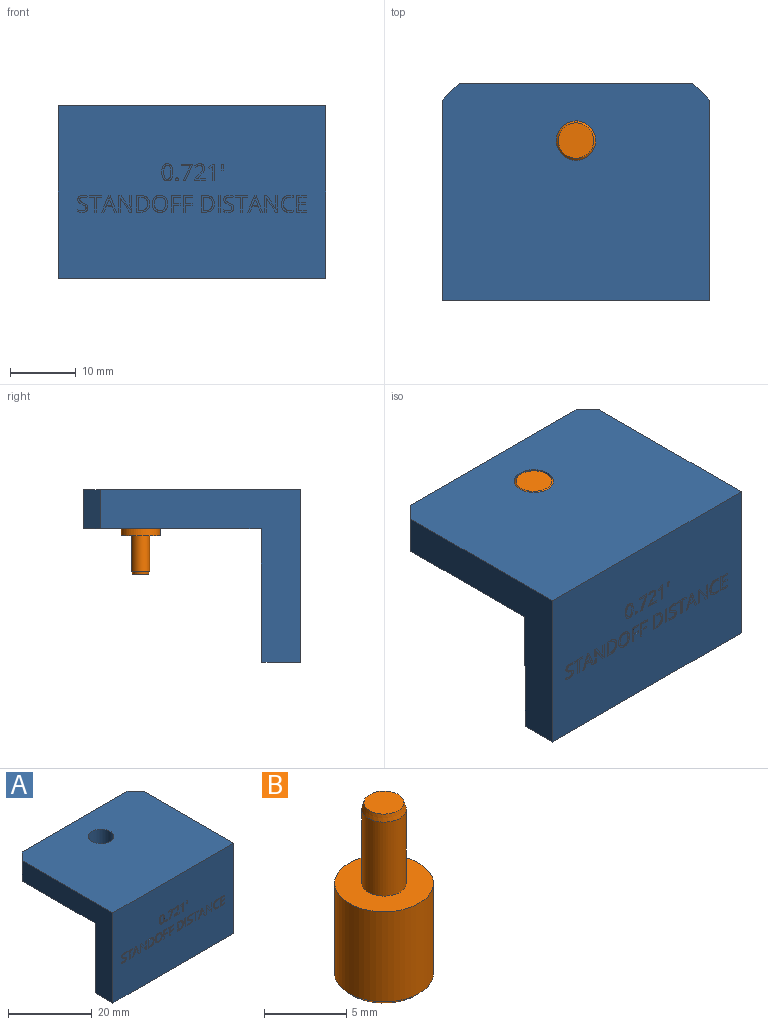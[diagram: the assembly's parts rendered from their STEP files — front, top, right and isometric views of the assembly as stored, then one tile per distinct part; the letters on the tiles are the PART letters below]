
ASSEMBLY  parts=2 mates=1
PART A: 322 faces, bbox 40.6x33x26.3 mm
  f0: plane 40.64x5.87mm, normal (0,0,-1), area 238.5mm2, adj f2,f3,f5,f320
  f1: plane 40.64x9.14mm, normal (0,1,0), area 371.6mm2, adj f2,f4,f5,f321
  f2: plane 30.48x26.32mm, normal (-1,0,0), area 303.3mm2, adj f0,f1,f3,f4,f7,f318,f320,f321
  f3: plane 40.64x26.32mm, normal (0,-1,0), area 1028.5mm2, adj f0,f2,f5,f7,f9,f10,f11,f12
  f4: plane 40.64x27.02mm, normal (0,0,-1), area 1063.4mm2, adj f1,f2,f5,f6,f8,f318,f319
  f5: plane 30.48x26.32mm, normal (1,0,0), area 303.3mm2, adj f0,f1,f3,f4,f7,f319,f320,f321
  f6: plane 35.56x6mm, normal (0,1,0), area 213.4mm2, adj f4,f7,f318,f319
  f7: plane 40.64x33.02mm, normal (0,0,1), area 1307.2mm2, adj f2,f3,f5,f6,f8,f318,f319
  f8: cylinder r=3mm len=6mm, axis (0,0,1), area 113.1mm2, adj f4,f7
  f9: extruded ~0.18x0.05mm, area 0mm2, adj f3,f10,f16,f17
  f10: extruded ~0.18x0.06mm, area 0mm2, adj f3,f9,f11,f17
  f11: extruded ~0.15x0.05mm, area 0mm2, adj f3,f10,f12,f17
  f12: extruded ~0.16x0.06mm, area 0mm2, adj f3,f11,f13,f17
  f13: extruded ~0.17x0.06mm, area 0mm2, adj f3,f12,f14,f17
  f14: extruded ~0.18x0.06mm, area 0mm2, adj f3,f13,f15,f17
  f15: extruded ~0.16x0.06mm, area 0mm2, adj f3,f14,f16,f17
  f16: extruded ~0.15x0.06mm, area 0mm2, adj f3,f9,f15,f17
  f17: plane 0.47x0.42mm, normal (0,-1,0), area 0.2mm2, adj f9,f10,f11,f12,f13,f14,f15,f16
  f18: plane 0.78x0.29mm, normal (0.94,0,0.35), area 0mm2, adj f19,f30,f31,f312
  f19: plane 0.81x0.03mm, normal (0,0,-1), area 0mm2, adj f18,f20,f31,f312
  f20: plane 0.78x0.3mm, normal (-0.94,0,0.35), area 0mm2, adj f19,f21,f31,f312
  f21: extruded ~0.36x0.11mm, area 0mm2, adj f20,f30,f31,f312
  f22: plane 0.8x0.31mm, normal (0.93,0,0.36), area 0mm2, adj f3,f23,f29,f31
  f23: plane 0.3x0.03mm, normal (0,0,1), area 0mm2, adj f3,f22,f24,f31
  f24: plane 2.53x0.99mm, normal (-0.93,0,-0.36), area 0.1mm2, adj f3,f23,f25,f31
  f25: plane 0.25x0.03mm, normal (0,0,-1), area 0mm2, adj f3,f24,f26,f31
  f26: plane 2.53x1mm, normal (0.93,0,-0.37), area 0.1mm2, adj f3,f25,f27,f31
  f27: plane 0.3x0.03mm, normal (0,0,1), area 0mm2, adj f3,f26,f28,f31
  f28: plane 0.8x0.31mm, normal (-0.93,0,0.36), area 0mm2, adj f3,f27,f29,f31
  f29: plane 1.01x0.03mm, normal (0,0,1), area 0mm2, adj f3,f22,f28,f31
  f30: extruded ~0.36x0.12mm, area 0mm2, adj f18,f21,f31,f312
  f31: plane 2.53x2.23mm, normal (0,-1,0), area 1.6mm2, adj f18,f19,f20,f21,f22,f23,f24,f25
  f32: extruded ~0.74x0.25mm, area 0mm2, adj f33,f45,f46,f313
  f33: extruded ~0.76x0.26mm, area 0mm2, adj f32,f34,f46,f313
  f34: extruded ~0.79x0.26mm, area 0mm2, adj f33,f35,f46,f313
  f35: plane 0.36x0.03mm, normal (0,0,-1), area 0mm2, adj f34,f36,f46,f313
  f36: plane 2.01x0.03mm, normal (-1,0,0), area 0.1mm2, adj f35,f37,f46,f313
  f37: plane 0.43x0.03mm, normal (0,0,1), area 0mm2, adj f36,f45,f46,f313
  f38: extruded ~0.95x0.34mm, area 0mm2, adj f3,f39,f44,f46
  f39: extruded ~0.91x0.33mm, area 0mm2, adj f3,f38,f40,f46
  f40: extruded ~0.91x0.33mm, area 0mm2, adj f3,f39,f41,f46
  f41: plane 0.77x0.03mm, normal (0,0,-1), area 0mm2, adj f3,f40,f42,f46
  f42: plane 2.52x0.03mm, normal (1,0,0), area 0.1mm2, adj f3,f41,f43,f46
  f43: plane 0.7x0.03mm, normal (0,0,1), area 0mm2, adj f3,f42,f44,f46
  f44: extruded ~0.97x0.33mm, area 0mm2, adj f3,f38,f43,f46
  f45: extruded ~0.74x0.25mm, area 0mm2, adj f32,f37,f46,f313
  f46: plane 2.52x2.01mm, normal (0,-1,0), area 2mm2, adj f32,f33,f34,f35,f36,f37,f38,f39
  f47: extruded ~0.78x0.22mm, area 0mm2, adj f48,f62,f63,f314
  f48: extruded ~0.77x0.22mm, area 0mm2, adj f47,f49,f63,f314
  f49: extruded ~0.64x0.26mm, area 0mm2, adj f48,f50,f63,f314
  f50: extruded ~0.63x0.26mm, area 0mm2, adj f49,f51,f63,f314
  f51: extruded ~0.77x0.21mm, area 0mm2, adj f50,f52,f63,f314
  f52: extruded ~0.78x0.21mm, area 0mm2, adj f51,f53,f63,f314
  f53: extruded ~0.63x0.26mm, area 0mm2, adj f52,f62,f63,f314
  f54: extruded ~0.95x0.31mm, area 0mm2, adj f3,f55,f61,f63
  f55: extruded ~0.95x0.31mm, area 0mm2, adj f3,f54,f56,f63
  f56: extruded ~0.85x0.34mm, area 0mm2, adj f3,f55,f57,f63
  f57: extruded ~0.86x0.34mm, area 0mm2, adj f3,f56,f58,f63
  f58: extruded ~0.95x0.3mm, area 0mm2, adj f3,f57,f59,f63
  f59: extruded ~0.96x0.3mm, area 0mm2, adj f3,f58,f60,f63
  f60: extruded ~0.86x0.34mm, area 0mm2, adj f3,f59,f61,f63
  f61: extruded ~0.85x0.35mm, area 0mm2, adj f3,f54,f60,f63
  f62: extruded ~0.63x0.26mm, area 0mm2, adj f47,f53,f63,f314
  f63: plane 2.59x2.32mm, normal (0,-1,0), area 2mm2, adj f47,f48,f49,f50,f51,f52,f53,f54
  f64: extruded ~0.74x0.25mm, area 0mm2, adj f65,f77,f78,f315
  f65: extruded ~0.76x0.26mm, area 0mm2, adj f64,f66,f78,f315
  f66: extruded ~0.79x0.26mm, area 0mm2, adj f65,f67,f78,f315
  f67: plane 0.36x0.03mm, normal (0,0,-1), area 0mm2, adj f66,f68,f78,f315
  f68: plane 2.01x0.03mm, normal (-1,0,0), area 0.1mm2, adj f67,f69,f78,f315
  f69: plane 0.43x0.03mm, normal (0,0,1), area 0mm2, adj f68,f77,f78,f315
  f70: extruded ~0.95x0.34mm, area 0mm2, adj f3,f71,f76,f78
  f71: extruded ~0.91x0.33mm, area 0mm2, adj f3,f70,f72,f78
  f72: extruded ~0.91x0.33mm, area 0mm2, adj f3,f71,f73,f78
  f73: plane 0.77x0.03mm, normal (0,0,-1), area 0mm2, adj f3,f72,f74,f78
  f74: plane 2.52x0.03mm, normal (1,0,0), area 0.1mm2, adj f3,f73,f75,f78
  f75: plane 0.7x0.03mm, normal (0,0,1), area 0mm2, adj f3,f74,f76,f78
  f76: extruded ~0.97x0.33mm, area 0mm2, adj f3,f70,f75,f78
  f77: extruded ~0.74x0.25mm, area 0mm2, adj f64,f69,f78,f315
  f78: plane 2.52x2.01mm, normal (0,-1,0), area 2mm2, adj f64,f65,f66,f67,f68,f69,f70,f71
  f79: plane 0.78x0.29mm, normal (0.94,0,0.35), area 0mm2, adj f80,f91,f92,f316
  f80: plane 0.81x0.03mm, normal (0,0,-1), area 0mm2, adj f79,f81,f92,f316
  f81: plane 0.78x0.3mm, normal (-0.94,0,0.35), area 0mm2, adj f80,f82,f92,f316
  f82: extruded ~0.36x0.11mm, area 0mm2, adj f81,f91,f92,f316
  f83: plane 0.8x0.31mm, normal (0.93,0,0.36), area 0mm2, adj f3,f84,f90,f92
  f84: plane 0.3x0.03mm, normal (0,0,1), area 0mm2, adj f3,f83,f85,f92
  f85: plane 2.53x0.99mm, normal (-0.93,0,-0.36), area 0.1mm2, adj f3,f84,f86,f92
  f86: plane 0.25x0.03mm, normal (0,0,-1), area 0mm2, adj f3,f85,f87,f92
  f87: plane 2.53x1mm, normal (0.93,0,-0.37), area 0.1mm2, adj f3,f86,f88,f92
  f88: plane 0.3x0.03mm, normal (0,0,1), area 0mm2, adj f3,f87,f89,f92
  f89: plane 0.8x0.31mm, normal (-0.93,0,0.36), area 0mm2, adj f3,f88,f90,f92
  f90: plane 1.01x0.03mm, normal (0,0,1), area 0mm2, adj f3,f83,f89,f92
  f91: extruded ~0.36x0.12mm, area 0mm2, adj f79,f82,f92,f316
  f92: plane 2.53x2.23mm, normal (0,-1,0), area 1.6mm2, adj f79,f80,f81,f82,f83,f84,f85,f86
  f93: plane 2.26x1.04mm, normal (0.91,0,-0.42), area 0.1mm2, adj f3,f94,f99,f100
  f94: plane 0.32x0.03mm, normal (0,0,1), area 0mm2, adj f3,f93,f95,f100
  f95: plane 2.29x1.03mm, normal (-0.91,0,0.41), area 0.1mm2, adj f3,f94,f96,f100
  f96: plane 0.23x0.03mm, normal (-1,0,0), area 0mm2, adj f3,f95,f97,f100
  f97: plane 1.68x0.03mm, normal (0,0,-1), area 0mm2, adj f3,f96,f98,f100
  f98: plane 0.26x0.03mm, normal (1,0,0), area 0mm2, adj f3,f97,f99,f100
  f99: plane 1.37x0.03mm, normal (0,0,1), area 0mm2, adj f3,f93,f98,f100
  f100: plane 2.52x1.68mm, normal (0,-1,0), area 1.1mm2, adj f93,f94,f95,f96,f97,f98,f99
  f101: plane 1.66x0.03mm, normal (0,0,1), area 0mm2, adj f3,f102,f120,f121
  f102: plane 0.27x0.03mm, normal (-1,0,0), area 0mm2, adj f3,f101,f103,f121
  f103: plane 1.3x0.03mm, normal (0,0,-1), area 0mm2, adj f3,f102,f104,f121
  f104: plane 0.03x0.01mm, normal (-1,0,0), area 0mm2, adj f3,f103,f105,f121
  f105: plane 0.55x0.54mm, normal (-0.7,0,0.71), area 0mm2, adj f3,f104,f106,f121
  f106: extruded ~0.59x0.5mm, area 0mm2, adj f3,f105,f107,f121
  f107: extruded ~0.47x0.13mm, area 0mm2, adj f3,f106,f108,f121
  f108: extruded ~0.49x0.2mm, area 0mm2, adj f3,f107,f109,f121
  f109: extruded ~0.56x0.18mm, area 0mm2, adj f3,f108,f110,f121
  f110: extruded ~0.76x0.29mm, area 0mm2, adj f3,f109,f111,f121
  f111: plane 0.19x0.15mm, normal (0.79,0,0.61), area 0mm2, adj f3,f110,f112,f121
  f112: extruded ~0.31x0.19mm, area 0mm2, adj f3,f111,f113,f121
  f113: extruded ~0.3x0.05mm, area 0mm2, adj f3,f112,f114,f121
  f114: extruded ~0.34x0.12mm, area 0mm2, adj f3,f113,f115,f121
  f115: extruded ~0.32x0.12mm, area 0mm2, adj f3,f114,f116,f121
  f116: extruded ~0.27x0.05mm, area 0mm2, adj f3,f115,f117,f121
  f117: extruded ~0.26x0.14mm, area 0mm2, adj f3,f116,f118,f121
  f118: extruded ~0.44x0.4mm, area 0mm2, adj f3,f117,f119,f121
  f119: plane 0.67x0.66mm, normal (0.71,0,-0.71), area 0mm2, adj f3,f118,f120,f121
  f120: plane 0.25x0.03mm, normal (1,0,0), area 0mm2, adj f3,f101,f119,f121
  f121: plane 2.55x1.66mm, normal (0,-1,0), area 1.4mm2, adj f101,f102,f103,f104,f105,f106,f107,f108
  f122: plane 0.28x0.03mm, normal (0,0,1), area 0mm2, adj f3,f123,f130,f131
  f123: plane 2.52x0.03mm, normal (-1,0,0), area 0.1mm2, adj f3,f122,f124,f131
  f124: plane 0.24x0.03mm, normal (0,0,-1), area 0mm2, adj f3,f123,f125,f131
  f125: plane 0.67x0.52mm, normal (0.61,0,-0.79), area 0mm2, adj f3,f124,f126,f131
  f126: plane 0.2x0.15mm, normal (0.79,0,0.61), area 0mm2, adj f3,f125,f127,f131
  f127: extruded ~0.41x0.34mm, area 0mm2, adj f3,f126,f128,f131
  f128: extruded ~0.08x0.08mm, area 0mm2, adj f3,f127,f129,f131
  f129: extruded ~0.42x0.03mm, area 0mm2, adj f3,f128,f130,f131
  f130: plane 1.79x0.03mm, normal (1,0,0), area 0mm2, adj f3,f122,f129,f131
  f131: plane 2.52x0.91mm, normal (0,-1,0), area 0.9mm2, adj f122,f123,f124,f125,f126,f127,f128,f129
  f132: plane 0.91x0.07mm, normal (-1,0,0.08), area 0mm2, adj f3,f133,f135,f136
  f133: plane 0.32x0.03mm, normal (0,0,-1), area 0mm2, adj f3,f132,f134,f136
  f134: plane 0.91x0.07mm, normal (1,0,0.08), area 0mm2, adj f3,f133,f135,f136
  f135: plane 0.18x0.03mm, normal (0,0,1), area 0mm2, adj f3,f132,f134,f136
  f136: plane 0.91x0.32mm, normal (0,-1,0), area 0.2mm2, adj f132,f133,f134,f135
  f137: extruded ~0.52x0.24mm, area 0mm2, adj f3,f138,f161,f162
  f138: extruded ~0.42x0.15mm, area 0mm2, adj f3,f137,f139,f162
  f139: extruded ~0.55x0.3mm, area 0mm2, adj f3,f138,f140,f162
  f140: extruded ~0.35x0.15mm, area 0mm2, adj f3,f139,f141,f162
  f141: extruded ~0.16x0.15mm, area 0mm2, adj f3,f140,f142,f162
  f142: extruded ~0.21x0.05mm, area 0mm2, adj f3,f141,f143,f162
  f143: extruded ~0.28x0.13mm, area 0mm2, adj f3,f142,f144,f162
  f144: extruded ~0.36x0.1mm, area 0mm2, adj f3,f143,f145,f162
  f145: extruded ~0.61x0.13mm, area 0mm2, adj f3,f144,f146,f162
  f146: plane 0.25x0.09mm, normal (-0.94,0,0.34), area 0mm2, adj f3,f145,f147,f162
  f147: extruded ~0.69x0.14mm, area 0mm2, adj f3,f146,f148,f162
  f148: extruded ~0.58x0.17mm, area 0mm2, adj f3,f147,f149,f162
  f149: extruded ~0.46x0.22mm, area 0mm2, adj f3,f148,f150,f162
  f150: extruded ~0.45x0.15mm, area 0mm2, adj f3,f149,f151,f162
  f151: extruded ~0.5x0.3mm, area 0mm2, adj f3,f150,f152,f162
  f152: extruded ~0.37x0.16mm, area 0mm2, adj f3,f151,f153,f162
  f153: extruded ~0.18x0.15mm, area 0mm2, adj f3,f152,f154,f162
  f154: extruded ~0.21x0.05mm, area 0mm2, adj f3,f153,f155,f162
  f155: extruded ~0.31x0.15mm, area 0mm2, adj f3,f154,f156,f162
  f156: extruded ~0.44x0.11mm, area 0mm2, adj f3,f155,f157,f162
  f157: extruded ~0.36x0.04mm, area 0mm2, adj f3,f156,f158,f162
  f158: extruded ~0.34x0.1mm, area 0mm2, adj f3,f157,f159,f162
  f159: plane 0.28x0.03mm, normal (1,0,0), area 0mm2, adj f3,f158,f160,f162
  f160: extruded ~0.69x0.12mm, area 0mm2, adj f3,f159,f161,f162
  f161: extruded ~0.65x0.19mm, area 0mm2, adj f3,f137,f160,f162
  f162: plane 2.59x1.58mm, normal (0,-1,0), area 1.5mm2, adj f137,f138,f139,f140,f141,f142,f143,f144
  f163: plane 0.29x0.03mm, normal (0,0,1), area 0mm2, adj f3,f164,f170,f171
  f164: plane 2.26x0.03mm, normal (-1,0,0), area 0.1mm2, adj f3,f163,f165,f171
  f165: plane 0.8x0.03mm, normal (0,0,1), area 0mm2, adj f3,f164,f166,f171
  f166: plane 0.26x0.03mm, normal (-1,0,0), area 0mm2, adj f3,f165,f167,f171
  f167: plane 1.89x0.03mm, normal (0,0,-1), area 0mm2, adj f3,f166,f168,f171
  f168: plane 0.26x0.03mm, normal (1,0,0), area 0mm2, adj f3,f167,f169,f171
  f169: plane 0.8x0.03mm, normal (0,0,1), area 0mm2, adj f3,f168,f170,f171
  f170: plane 2.26x0.03mm, normal (1,0,0), area 0.1mm2, adj f3,f163,f169,f171
  f171: plane 2.52x1.89mm, normal (0,-1,0), area 1.2mm2, adj f163,f164,f165,f166,f167,f168,f169,f170
  f172: plane 0.33x0.03mm, normal (0,0,1), area 0mm2, adj f3,f173,f186,f187
  f173: plane 2.52x0.03mm, normal (-1,0,0), area 0.1mm2, adj f3,f172,f174,f187
  f174: plane 0.27x0.03mm, normal (0,0,-1), area 0mm2, adj f3,f173,f175,f187
  f175: plane 1.45x0.03mm, normal (1,0,0), area 0mm2, adj f3,f174,f176,f187
  f176: extruded ~0.36x0.03mm, area 0mm2, adj f3,f175,f177,f187
  f177: extruded ~0.3x0.03mm, area 0mm2, adj f3,f176,f178,f187
  f178: plane 0.03x0.01mm, normal (0,0,-1), area 0mm2, adj f3,f177,f179,f187
  f179: plane 2.11x1.37mm, normal (-0.84,0,-0.55), area 0.1mm2, adj f3,f178,f180,f187
  f180: plane 0.33x0.03mm, normal (0,0,-1), area 0mm2, adj f3,f179,f181,f187
  f181: plane 2.52x0.03mm, normal (1,0,0), area 0.1mm2, adj f3,f180,f182,f187
  f182: plane 0.27x0.03mm, normal (0,0,1), area 0mm2, adj f3,f181,f183,f187
  f183: plane 1.43x0.03mm, normal (-1,0,0), area 0mm2, adj f3,f182,f184,f187
  f184: extruded ~0.68x0.03mm, area 0mm2, adj f3,f183,f185,f187
  f185: plane 0.03x0.01mm, normal (0,0,1), area 0mm2, adj f3,f184,f186,f187
  f186: plane 2.11x1.38mm, normal (0.84,0,0.55), area 0.1mm2, adj f3,f172,f185,f187
  f187: plane 2.52x1.97mm, normal (0,-1,0), area 2.1mm2, adj f172,f173,f174,f175,f176,f177,f178,f179
  f188: plane 0.29x0.03mm, normal (0,0,1), area 0mm2, adj f3,f189,f197,f198
  f189: plane 1.08x0.03mm, normal (-1,0,0), area 0mm2, adj f3,f188,f190,f198
  f190: plane 1.04x0.03mm, normal (0,0,1), area 0mm2, adj f3,f189,f191,f198
  f191: plane 0.26x0.03mm, normal (-1,0,0), area 0mm2, adj f3,f190,f192,f198
  f192: plane 1.04x0.03mm, normal (0,0,-1), area 0mm2, adj f3,f191,f193,f198
  f193: plane 0.92x0.03mm, normal (-1,0,0), area 0mm2, adj f3,f192,f194,f198
  f194: plane 1.11x0.03mm, normal (0,0,1), area 0mm2, adj f3,f193,f195,f198
  f195: plane 0.26x0.03mm, normal (-1,0,0), area 0mm2, adj f3,f194,f196,f198
  f196: plane 1.4x0.03mm, normal (0,0,-1), area 0mm2, adj f3,f195,f197,f198
  f197: plane 2.52x0.03mm, normal (1,0,0), area 0.1mm2, adj f3,f188,f196,f198
  f198: plane 2.52x1.4mm, normal (0,-1,0), area 1.3mm2, adj f188,f189,f190,f191,f192,f193,f194,f195
  f199: plane 0.33x0.03mm, normal (0,0,1), area 0mm2, adj f3,f200,f213,f214
  f200: plane 2.52x0.03mm, normal (-1,0,0), area 0.1mm2, adj f3,f199,f201,f214
  f201: plane 0.27x0.03mm, normal (0,0,-1), area 0mm2, adj f3,f200,f202,f214
  f202: plane 1.45x0.03mm, normal (1,0,0), area 0mm2, adj f3,f201,f203,f214
  f203: extruded ~0.36x0.03mm, area 0mm2, adj f3,f202,f204,f214
  f204: extruded ~0.3x0.03mm, area 0mm2, adj f3,f203,f205,f214
  f205: plane 0.03x0.01mm, normal (0,0,-1), area 0mm2, adj f3,f204,f206,f214
  f206: plane 2.11x1.37mm, normal (-0.84,0,-0.55), area 0.1mm2, adj f3,f205,f207,f214
  f207: plane 0.33x0.03mm, normal (0,0,-1), area 0mm2, adj f3,f206,f208,f214
  f208: plane 2.52x0.03mm, normal (1,0,0), area 0.1mm2, adj f3,f207,f209,f214
  f209: plane 0.27x0.03mm, normal (0,0,1), area 0mm2, adj f3,f208,f210,f214
  f210: plane 1.43x0.03mm, normal (-1,0,0), area 0mm2, adj f3,f209,f211,f214
  f211: extruded ~0.68x0.03mm, area 0mm2, adj f3,f210,f212,f214
  f212: plane 0.03x0.01mm, normal (0,0,1), area 0mm2, adj f3,f211,f213,f214
  f213: plane 2.11x1.38mm, normal (0.84,0,0.55), area 0.1mm2, adj f3,f199,f212,f214
  f214: plane 2.52x1.97mm, normal (0,-1,0), area 2.1mm2, adj f199,f200,f201,f202,f203,f204,f205,f206
  f215: extruded ~0.66x0.28mm, area 0mm2, adj f3,f216,f229,f230
  f216: extruded ~0.57x0.13mm, area 0mm2, adj f3,f215,f217,f230
  f217: plane 0.25x0.12mm, normal (-0.9,0,0.44), area 0mm2, adj f3,f216,f218,f230
  f218: extruded ~0.69x0.14mm, area 0mm2, adj f3,f217,f219,f230
  f219: extruded ~0.65x0.16mm, area 0mm2, adj f3,f218,f220,f230
  f220: extruded ~0.45x0.42mm, area 0mm2, adj f3,f219,f221,f230
  f221: extruded ~0.68x0.15mm, area 0mm2, adj f3,f220,f222,f230
  f222: extruded ~0.96x0.3mm, area 0mm2, adj f3,f221,f223,f230
  f223: extruded ~0.86x0.34mm, area 0mm2, adj f3,f222,f224,f230
  f224: extruded ~0.65x0.1mm, area 0mm2, adj f3,f223,f225,f230
  f225: plane 0.26x0.03mm, normal (-1,0,0), area 0mm2, adj f3,f224,f226,f230
  f226: extruded ~0.6x0.1mm, area 0mm2, adj f3,f225,f227,f230
  f227: extruded ~0.66x0.27mm, area 0mm2, adj f3,f226,f228,f230
  f228: extruded ~0.76x0.23mm, area 0mm2, adj f3,f227,f229,f230
  f229: extruded ~0.76x0.24mm, area 0mm2, adj f3,f215,f228,f230
  f230: plane 2.59x1.91mm, normal (0,-1,0), area 1.4mm2, adj f215,f216,f217,f218,f219,f220,f221,f222
  f231: plane 1.4x0.03mm, normal (0,0,1), area 0mm2, adj f3,f232,f242,f243
  f232: plane 0.26x0.03mm, normal (-1,0,0), area 0mm2, adj f3,f231,f233,f243
  f233: plane 1.11x0.03mm, normal (0,0,-1), area 0mm2, adj f3,f232,f234,f243
  f234: plane 0.93x0.03mm, normal (-1,0,0), area 0mm2, adj f3,f233,f235,f243
  f235: plane 1.04x0.03mm, normal (0,0,1), area 0mm2, adj f3,f234,f236,f243
  f236: plane 0.26x0.03mm, normal (-1,0,0), area 0mm2, adj f3,f235,f237,f243
  f237: plane 1.04x0.03mm, normal (0,0,-1), area 0mm2, adj f3,f236,f238,f243
  f238: plane 0.81x0.03mm, normal (-1,0,0), area 0mm2, adj f3,f237,f239,f243
  f239: plane 1.11x0.03mm, normal (0,0,1), area 0mm2, adj f3,f238,f240,f243
  f240: plane 0.26x0.03mm, normal (-1,0,0), area 0mm2, adj f3,f239,f241,f243
  f241: plane 1.4x0.03mm, normal (0,0,-1), area 0mm2, adj f3,f240,f242,f243
  f242: plane 2.52x0.03mm, normal (1,0,0), area 0.1mm2, adj f3,f231,f241,f243
  f243: plane 2.52x1.4mm, normal (0,-1,0), area 1.6mm2, adj f231,f232,f233,f234,f235,f236,f237,f238
  f244: extruded ~0.8x0.13mm, area 0mm2, adj f245,f259,f260,f317
  f245: extruded ~0.8x0.13mm, area 0mm2, adj f244,f246,f260,f317
  f246: extruded ~0.41x0.25mm, area 0mm2, adj f245,f247,f260,f317
  f247: extruded ~0.41x0.25mm, area 0mm2, adj f246,f248,f260,f317
  f248: extruded ~0.8x0.13mm, area 0mm2, adj f247,f249,f260,f317
  f249: extruded ~0.8x0.13mm, area 0mm2, adj f248,f250,f260,f317
  f250: extruded ~0.41x0.25mm, area 0mm2, adj f249,f259,f260,f317
  f251: extruded ~0.98x0.21mm, area 0mm2, adj f3,f252,f258,f260
  f252: extruded ~0.96x0.21mm, area 0mm2, adj f3,f251,f253,f260
  f253: extruded ~0.62x0.33mm, area 0mm2, adj f3,f252,f254,f260
  f254: extruded ~0.63x0.32mm, area 0mm2, adj f3,f253,f255,f260
  f255: extruded ~0.98x0.21mm, area 0mm2, adj f3,f254,f256,f260
  f256: extruded ~0.97x0.21mm, area 0mm2, adj f3,f255,f257,f260
  f257: extruded ~0.62x0.33mm, area 0mm2, adj f3,f256,f258,f260
  f258: extruded ~0.63x0.32mm, area 0mm2, adj f3,f251,f257,f260
  f259: extruded ~0.41x0.25mm, area 0mm2, adj f244,f250,f260,f317
  f260: plane 2.59x1.67mm, normal (0,-1,0), area 1.7mm2, adj f244,f245,f246,f247,f248,f249,f250,f251
  f261: plane 0.29x0.03mm, normal (0,0,1), area 0mm2, adj f3,f262,f268,f269
  f262: plane 2.26x0.03mm, normal (-1,0,0), area 0.1mm2, adj f3,f261,f263,f269
  f263: plane 0.8x0.03mm, normal (0,0,1), area 0mm2, adj f3,f262,f264,f269
  f264: plane 0.26x0.03mm, normal (-1,0,0), area 0mm2, adj f3,f263,f265,f269
  f265: plane 1.89x0.03mm, normal (0,0,-1), area 0mm2, adj f3,f264,f266,f269
  f266: plane 0.26x0.03mm, normal (1,0,0), area 0mm2, adj f3,f265,f267,f269
  f267: plane 0.8x0.03mm, normal (0,0,1), area 0mm2, adj f3,f266,f268,f269
  f268: plane 2.26x0.03mm, normal (1,0,0), area 0.1mm2, adj f3,f261,f267,f269
  f269: plane 2.52x1.89mm, normal (0,-1,0), area 1.2mm2, adj f261,f262,f263,f264,f265,f266,f267,f268
  f270: extruded ~0.52x0.24mm, area 0mm2, adj f3,f271,f294,f295
  f271: extruded ~0.42x0.15mm, area 0mm2, adj f3,f270,f272,f295
  f272: extruded ~0.55x0.3mm, area 0mm2, adj f3,f271,f273,f295
  f273: extruded ~0.35x0.15mm, area 0mm2, adj f3,f272,f274,f295
  f274: extruded ~0.16x0.15mm, area 0mm2, adj f3,f273,f275,f295
  f275: extruded ~0.21x0.05mm, area 0mm2, adj f3,f274,f276,f295
  f276: extruded ~0.28x0.13mm, area 0mm2, adj f3,f275,f277,f295
  f277: extruded ~0.36x0.1mm, area 0mm2, adj f3,f276,f278,f295
  f278: extruded ~0.61x0.13mm, area 0mm2, adj f3,f277,f279,f295
  f279: plane 0.25x0.09mm, normal (-0.94,0,0.34), area 0mm2, adj f3,f278,f280,f295
  f280: extruded ~0.69x0.14mm, area 0mm2, adj f3,f279,f281,f295
  f281: extruded ~0.58x0.17mm, area 0mm2, adj f3,f280,f282,f295
  f282: extruded ~0.46x0.22mm, area 0mm2, adj f3,f281,f283,f295
  f283: extruded ~0.45x0.15mm, area 0mm2, adj f3,f282,f284,f295
  f284: extruded ~0.5x0.3mm, area 0mm2, adj f3,f283,f285,f295
  f285: extruded ~0.37x0.16mm, area 0mm2, adj f3,f284,f286,f295
  f286: extruded ~0.18x0.15mm, area 0mm2, adj f3,f285,f287,f295
  f287: extruded ~0.21x0.05mm, area 0mm2, adj f3,f286,f288,f295
  f288: extruded ~0.31x0.15mm, area 0mm2, adj f3,f287,f289,f295
  f289: extruded ~0.44x0.11mm, area 0mm2, adj f3,f288,f290,f295
  f290: extruded ~0.36x0.04mm, area 0mm2, adj f3,f289,f291,f295
  f291: extruded ~0.34x0.1mm, area 0mm2, adj f3,f290,f292,f295
  f292: plane 0.28x0.03mm, normal (1,0,0), area 0mm2, adj f3,f291,f293,f295
  f293: extruded ~0.69x0.12mm, area 0mm2, adj f3,f292,f294,f295
  f294: extruded ~0.65x0.19mm, area 0mm2, adj f3,f270,f293,f295
  f295: plane 2.59x1.58mm, normal (0,-1,0), area 1.5mm2, adj f270,f271,f272,f273,f274,f275,f276,f277
  f296: plane 2.52x0.03mm, normal (1,0,0), area 0.1mm2, adj f3,f297,f299,f300
  f297: plane 0.29x0.03mm, normal (0,0,1), area 0mm2, adj f3,f296,f298,f300
  f298: plane 2.52x0.03mm, normal (-1,0,0), area 0.1mm2, adj f3,f297,f299,f300
  f299: plane 0.29x0.03mm, normal (0,0,-1), area 0mm2, adj f3,f296,f298,f300
  f300: plane 2.52x0.29mm, normal (0,-1,0), area 0.7mm2, adj f296,f297,f298,f299
  f301: plane 0.29x0.03mm, normal (0,0,1), area 0mm2, adj f3,f302,f310,f311
  f302: plane 1.08x0.03mm, normal (-1,0,0), area 0mm2, adj f3,f301,f303,f311
  f303: plane 1.04x0.03mm, normal (0,0,1), area 0mm2, adj f3,f302,f304,f311
  f304: plane 0.26x0.03mm, normal (-1,0,0), area 0mm2, adj f3,f303,f305,f311
  f305: plane 1.04x0.03mm, normal (0,0,-1), area 0mm2, adj f3,f304,f306,f311
  f306: plane 0.92x0.03mm, normal (-1,0,0), area 0mm2, adj f3,f305,f307,f311
  f307: plane 1.11x0.03mm, normal (0,0,1), area 0mm2, adj f3,f306,f308,f311
  f308: plane 0.26x0.03mm, normal (-1,0,0), area 0mm2, adj f3,f307,f309,f311
  f309: plane 1.4x0.03mm, normal (0,0,-1), area 0mm2, adj f3,f308,f310,f311
  f310: plane 2.52x0.03mm, normal (1,0,0), area 0.1mm2, adj f3,f301,f309,f311
  f311: plane 2.52x1.4mm, normal (0,-1,0), area 1.3mm2, adj f301,f302,f303,f304,f305,f306,f307,f308
  f312: plane 1.14x0.81mm, normal (0,-1,0), area 0.4mm2, adj f18,f19,f20,f21,f30
  f313: plane 2.01x1.41mm, normal (0,-1,0), area 2.5mm2, adj f32,f33,f34,f35,f36,f37,f45
  f314: plane 2.07x1.7mm, normal (0,-1,0), area 2.9mm2, adj f47,f48,f49,f50,f51,f52,f53,f62
  f315: plane 2.01x1.41mm, normal (0,-1,0), area 2.5mm2, adj f64,f65,f66,f67,f68,f69,f77
  f316: plane 1.14x0.81mm, normal (0,-1,0), area 0.4mm2, adj f79,f80,f81,f82,f91
  f317: plane 2.1x1.08mm, normal (0,-1,0), area 1.9mm2, adj f244,f245,f246,f247,f248,f249,f250,f259
  f318: plane 6x2.54mm, normal (-0.71,0.71,0), area 21.6mm2, adj f2,f4,f6,f7
  f319: plane 6x2.54mm, normal (0.71,0.71,0), area 21.6mm2, adj f4,f5,f6,f7
  f320: plane 40.64x11.18mm, normal (0,1,0), area 454.2mm2, adj f0,f2,f5,f321
  f321: plane 40.64x0.13mm, normal (0,0,-1), area 5.4mm2, adj f1,f2,f5,f320
PART B: 7 faces, bbox 6x6x13 mm
  f0: plane 5.4x5.4mm, normal (0,0,-1), area 22.9mm2, adj f5
  f1: cylinder r=3mm len=6.7mm, axis (0,0,-1), area 126.3mm2, adj f2,f5
  f2: plane 6x6mm, normal (0,0,1), area 22.5mm2, adj f1,f3
  f3: cylinder r=1.35mm len=5.5mm, axis (0,0,-1), area 46.7mm2, adj f2,f6
  f4: plane 2.43x2.43mm, normal (0,0,1), area 4.6mm2, adj f6
  f5: cone r=2.7mm half-angle=45deg, axis (0,0,1), area 7.6mm2, adj f0,f1
  f6: cone r=1.35mm half-angle=15deg, axis (0,0,-1), area 4.2mm2, adj f3,f4
PLACE A t=(4.06,2.66,0.47)mm fixed
PLACE B rot(axis=(1,0,0),180deg) t=(2.45,10.46,-0.53)mm
MATE fastened B.f1 <-> A.f8  axis (0,0,1) through (4.06,10.46,6.47)mm
